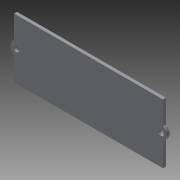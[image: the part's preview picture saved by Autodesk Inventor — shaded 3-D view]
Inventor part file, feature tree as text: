
AUTODESK INVENTOR PART (.ipt)
format: ipt  version: 2014 SP1 (Build 180222100, 222)  size: 79,872 bytes
history: native  units: in
note: dims shown in document units (in); Inventor stores cm internally (conversion verified against a paired STEP export)
features: extrude x1, sketch x1
ambient origin geometry x8: Origin, YZ Plane, XZ Plane, XY Plane, X Axis, Y Axis, Z Axis, Center Point
bodies: Solid1 (feature_tree)
feature tree (2):
  extrude  "Extrusion1"  Depth=1.0in
  sketch  "Sketch1"  dims[d0=2.5in d1=1.0in d4=0.094in d5=0.094in d6=0.05in d7=0.0in]
